# Revit family: IS_Connect_E5672_BIM_DE
name_source: partatom
category: Plumbing Fixtures
revit_build: Autodesk Revit MEP 2016 (Build: 20161004_0715(x64)
units: mm (PartAtom-declared; Revit-internal decimal feet)

## family parameters
Always vertical = No
Cut with Voids When Loaded = No
OmniClass Number = 23.45.05.21.11.21
OmniClass Title = Urinals
Part Type = Normal
Room Calculation Point = No
Round Connector Dimension = Use Diameter
Shared = No
Work Plane-Based = No

## types (2) — shared parameters
Accessories = www.idealstandard.de\ersatzteile
AssetType = Fixed
BIMobject category = Urinals
BOSUseNativeGeometries = 1
Brand = Ideal Standard
Brand url = http://www.idealstandard.de
CodePerformance = DIN EN 13407 CL1 - I - 2C, DIN EN
ConnectionType = Plumbing
CurrencyUnit = €
CurrentRevision = 1
DurationUnit = Jaar
EAN code = https://5017830480518
Edition number = 1
ExpectedLife = 25
Features = CONNECT urinal 310x335mm, top inlet
IFC Classification = Sanitary Terminal
IfcExportAs = Sanitary terminal type
IfcExportType = URINAL
Installation instructions = http://www.idealstandard.it
InstallationInstructions = www.idealstandard.de\produkte
LinearUnits = millimetres
MaintenanceInformation = www.idealstandard.de
Manufacturer = http://www.idealstandard.de
Manufacturer name = Ideal Standard
ManufacturerURL = http://www.idealstandard.de
Material = Vitreous china
Material main = Ceramics
NBS Reference Code = 35-93-82
NBS Reference Description = Wall-Hung Urinals
Nominal height = 570
Nominal width = 310
NominalHeight = 571 mm
NominalLength = 337 mm
NominalWidth = 309 mm
OmniClass Code = 23-31 21 00
OmniClass Description = Urinals
Product Guid = ce44c6b4-f83e-42a2-830e-37d36d118179
Product SKU = E5672
Product certification = DIN EN 13407 CL1 - I - 2C, DIN EN
Product data url = https://bimobject.com
Product family = CONNECT
Product group = Urinal
Product name = CONNECT URINAL HO TI WHITE
Product url = http://www.idealstandard.it
ProductInformation = www.idealstandard.de/produkte
QR code = http://bimobject.com
Shape = Sculptured
Size = 309x337x571 mm
Space = Internal
SpareParts = www.idealstandard.de/ersatzteile
Technical description = http://www.idealstandard.it
URL = http://www.idealstandard.de
Uniclass 1.4 Code = L7217
Uniclass 1.4 Description = Urinals
Uniclass 2.0 Code = PR-35-93-82
Uniclass 2.0 Description = Wall-Hung Urinals
Uniclass 2015 Code = Pr_40_20_93_82
Uniclass 2015 Name = Wall-hung urinals
Uniclass2015Code = Pr_40_20_93_82
Uniclass2015Title = Wall-hung urinals
Uniclass2015Version = Products v1.1
VolumeUnits = Litres
Weight Net (Kg) = 15.5
zero-valued in all types: Cost, SpilloverLevel

## per-type parameters (varying)
| type | BIMObjectName | BarCode | Color | Finish | MainColor | Model | ModelNumber | Name | NettWeight |
| E567201 CONNECT urinal 310x335mm, top inlet | ISI_IdealStandard_Wall-hungurinals_CONNECT_E567201 | 5017830480518 | White | White | White | E567201 | E567201 | ISI_IdealStandard_Wall-hungurinals_CONNECT_E567201 | 13 kg |
| E5672MA CONNECT urinal 310x335mm, top inlet | ISI_IdealStandard_Wall-hungurinals_CONNECT_E5672MA | 5017830480525 | WHITE IP | WHITE IP | WHITE IP | E5672MA | E5672MA | ISI_IdealStandard_Wall-hungurinals_CONNECT_E5672MA | 15,5 kg |

note: column(s) folded — value = type name in every type: Description, ModelReference

## geometry (parser evidence)
native form markers: Blend x4, Sweep x1
no freeform markers — native parametric forms only
